# Revit family: console with 2 cutouts for bowl with tap hole
name_source: partatom
category: Furniture
units: mm (PartAtom-declared; Revit-internal decimal feet)

## family parameters
Always vertical = Yes
Cut with Voids When Loaded = No
OmniClass Number = 23.21.19.15.33.13
Room Calculation Point = No
Shared = Yes
Work Plane-Based = No

## types (16) — shared parameters
BIMOBJECT = Sanitary: Compound units
CATALOG = Hansgrohe
DESIGN = Germany
ETIM = EC011381 | Bathroom furniture set
IFC = Furnishing element
L1 = 140
MASTERFORMAT = 12 35 30.23 | Bathroom Casework
Manufacturer = Hansgrohe
NBSYN = $BASENUMBER.-$ARTNR.-$SURFACE.-$LODLEVEL.
NN = Console with 2 cutouts for bowl with tap hole
OBJECTTYPE = Object (single object)
OMNICLASS = 23-19 31 17 11 | Bathroom Units
PRODUCTFAMILY = Xelu Q
PRODUCTGROUP = console
PRODUCTURL = https://pro.hansgrohe.com
REGIONSET = Worldwide
UNICLASS2015 = Pr_40_20_76_94 | Vanity units
UNIFORMATII = E2010 | Fixed Furnishings
UNSPSC = 56 | Furniture and Furnishings

## per-type parameters (varying)
| type | ARTNR | BASENUMBER | GTINCODE | L | LINA | LL | LODLEVEL | Model | NAME | NB | PERMALINK | SPECIFICATION | SURFACE | WEIGHT |
| Console 1360_550 with 2 cutouts for bowl with tap hole-54125050-GLOSSY_WHITE-200 | 54125050 | Console 1360/550 with 2 cutouts for bowl with tap hole | 4059625457856 | 1360 | Console 1360/550 with 2 cutouts for bowl with tap hole-54125050-GLOSSY_WHITE-200 | 270 | 200 | Console 1360/550 with 2 cutouts for bowl with tap hole-54125050-GLOSSY_WHITE-200 | Xelu Q Console 1360/550 with 2 cutouts for bowl with tap hole | Console 1360/550 with 2 cutouts for bowl with tap hole-54125050-GLOSSY_WHITE-200 | 54125XXX | Surfaces:    - 54125050 High Gloss White  - 54125910 Diamond Matt Grey  - 54125230 Natural Oak  - 54125630 Dark Walnut     Specification: | GLOSSY_WHITE | 12 |
| Console 1360_550 with 2 cutouts for bowl with tap hole-54125050-GLOSSY_WHITE-400 | 54125050 | Console 1360/550 with 2 cutouts for bowl with tap hole | 4059625457856 | 1360 | Console 1360/550 with 2 cutouts for bowl with tap hole-54125050-GLOSSY_WHITE-400 | 270 | 400 | Console 1360/550 with 2 cutouts for bowl with tap hole-54125050-GLOSSY_WHITE-400 | Xelu Q Console 1360/550 with 2 cutouts for bowl with tap hole | Console 1360/550 with 2 cutouts for bowl with tap hole-54125050-GLOSSY_WHITE-400 | 54125XXX | Surfaces:    - 54125050 High Gloss White  - 54125910 Diamond Matt Grey  - 54125230 Natural Oak  - 54125630 Dark Walnut     Specification: | GLOSSY_WHITE | 12 |
| Console 1360_550 with 2 cutouts for bowl with tap hole-54125230-NATURAL_OAK-200 | 54125230 | Console 1360/550 with 2 cutouts for bowl with tap hole | 4059625457856 | 1360 | Console 1360/550 with 2 cutouts for bowl with tap hole-54125230-NATURAL_OAK-200 | 270 | 200 | Console 1360/550 with 2 cutouts for bowl with tap hole-54125230-NATURAL_OAK-200 | Xelu Q Console 1360/550 with 2 cutouts for bowl with tap hole | Console 1360/550 with 2 cutouts for bowl with tap hole-54125230-NATURAL_OAK-200 | 54125XXX | Surfaces:    - 54125050 High Gloss White  - 54125910 Diamond Matt Grey  - 54125230 Natural Oak  - 54125630 Dark Walnut     Specification: | NATURAL_OAK | 12 |
| Console 1360_550 with 2 cutouts for bowl with tap hole-54125230-NATURAL_OAK-400 | 54125230 | Console 1360/550 with 2 cutouts for bowl with tap hole | 4059625457856 | 1360 | Console 1360/550 with 2 cutouts for bowl with tap hole-54125230-NATURAL_OAK-400 | 270 | 400 | Console 1360/550 with 2 cutouts for bowl with tap hole-54125230-NATURAL_OAK-400 | Xelu Q Console 1360/550 with 2 cutouts for bowl with tap hole | Console 1360/550 with 2 cutouts for bowl with tap hole-54125230-NATURAL_OAK-400 | 54125XXX | Surfaces:    - 54125050 High Gloss White  - 54125910 Diamond Matt Grey  - 54125230 Natural Oak  - 54125630 Dark Walnut     Specification: | NATURAL_OAK | 12 |
| Console 1360_550 with 2 cutouts for bowl with tap hole-54125630-DARK_WALNUT-200 | 54125630 | Console 1360/550 with 2 cutouts for bowl with tap hole | 4059625457856 | 1360 | Console 1360/550 with 2 cutouts for bowl with tap hole-54125630-DARK_WALNUT-200 | 270 | 200 | Console 1360/550 with 2 cutouts for bowl with tap hole-54125630-DARK_WALNUT-200 | Xelu Q Console 1360/550 with 2 cutouts for bowl with tap hole | Console 1360/550 with 2 cutouts for bowl with tap hole-54125630-DARK_WALNUT-200 | 54125XXX | Surfaces:    - 54125050 High Gloss White  - 54125910 Diamond Matt Grey  - 54125230 Natural Oak  - 54125630 Dark Walnut     Specification: | DARK_WALNUT | 12 |
| Console 1360_550 with 2 cutouts for bowl with tap hole-54125630-DARK_WALNUT-400 | 54125630 | Console 1360/550 with 2 cutouts for bowl with tap hole | 4059625457856 | 1360 | Console 1360/550 with 2 cutouts for bowl with tap hole-54125630-DARK_WALNUT-400 | 270 | 400 | Console 1360/550 with 2 cutouts for bowl with tap hole-54125630-DARK_WALNUT-400 | Xelu Q Console 1360/550 with 2 cutouts for bowl with tap hole | Console 1360/550 with 2 cutouts for bowl with tap hole-54125630-DARK_WALNUT-400 | 54125XXX | Surfaces:    - 54125050 High Gloss White  - 54125910 Diamond Matt Grey  - 54125230 Natural Oak  - 54125630 Dark Walnut     Specification: | DARK_WALNUT | 12 |
| Console 1360_550 with 2 cutouts for bowl with tap hole-54125910-DIAMOND_GREY-200 | 54125910 | Console 1360/550 with 2 cutouts for bowl with tap hole | 4059625457856 | 1360 | Console 1360/550 with 2 cutouts for bowl with tap hole-54125910-DIAMOND_GREY-200 | 270 | 200 | Console 1360/550 with 2 cutouts for bowl with tap hole-54125910-DIAMOND_GREY-200 | Xelu Q Console 1360/550 with 2 cutouts for bowl with tap hole | Console 1360/550 with 2 cutouts for bowl with tap hole-54125910-DIAMOND_GREY-200 | 54125XXX | Surfaces:    - 54125050 High Gloss White  - 54125910 Diamond Matt Grey  - 54125230 Natural Oak  - 54125630 Dark Walnut     Specification: | DIAMOND_GREY | 12 |
| Console 1360_550 with 2 cutouts for bowl with tap hole-54125910-DIAMOND_GREY-400 | 54125910 | Console 1360/550 with 2 cutouts for bowl with tap hole | 4059625457856 | 1360 | Console 1360/550 with 2 cutouts for bowl with tap hole-54125910-DIAMOND_GREY-400 | 270 | 400 | Console 1360/550 with 2 cutouts for bowl with tap hole-54125910-DIAMOND_GREY-400 | Xelu Q Console 1360/550 with 2 cutouts for bowl with tap hole | Console 1360/550 with 2 cutouts for bowl with tap hole-54125910-DIAMOND_GREY-400 | 54125XXX | Surfaces:    - 54125050 High Gloss White  - 54125910 Diamond Matt Grey  - 54125230 Natural Oak  - 54125630 Dark Walnut     Specification: | DIAMOND_GREY | 12 |
| Console 1560_550 with 2 cutouts for bowl with tap hole-54126050-GLOSSY_WHITE-200 | 54126050 | Console 1560/550 with 2 cutouts for bowl with tap hole | 4059625458211 | 1560 | Console 1560/550 with 2 cutouts for bowl with tap hole-54126050-GLOSSY_WHITE-200 | 320 | 200 | Console 1560/550 with 2 cutouts for bowl with tap hole-54126050-GLOSSY_WHITE-200 | Xelu Q Console 1560/550 with 2 cutouts for bowl with tap hole | Console 1560/550 with 2 cutouts for bowl with tap hole-54126050-GLOSSY_WHITE-200 | 54126XXX | Surfaces:    - 54126050 High Gloss White  - 54126910 Diamond Matt Grey  - 54126230 Natural Oak  - 54126630 Dark Walnut      Specification: | GLOSSY_WHITE | 13.3 |
| Console 1560_550 with 2 cutouts for bowl with tap hole-54126050-GLOSSY_WHITE-400 | 54126050 | Console 1560/550 with 2 cutouts for bowl with tap hole | 4059625458211 | 1560 | Console 1560/550 with 2 cutouts for bowl with tap hole-54126050-GLOSSY_WHITE-400 | 320 | 400 | Console 1560/550 with 2 cutouts for bowl with tap hole-54126050-GLOSSY_WHITE-400 | Xelu Q Console 1560/550 with 2 cutouts for bowl with tap hole | Console 1560/550 with 2 cutouts for bowl with tap hole-54126050-GLOSSY_WHITE-400 | 54126XXX | Surfaces:    - 54126050 High Gloss White  - 54126910 Diamond Matt Grey  - 54126230 Natural Oak  - 54126630 Dark Walnut      Specification: | GLOSSY_WHITE | 13.3 |
| Console 1560_550 with 2 cutouts for bowl with tap hole-54126230-NATURAL_OAK-200 | 54126230 | Console 1560/550 with 2 cutouts for bowl with tap hole | 4059625458211 | 1560 | Console 1560/550 with 2 cutouts for bowl with tap hole-54126230-NATURAL_OAK-200 | 320 | 200 | Console 1560/550 with 2 cutouts for bowl with tap hole-54126230-NATURAL_OAK-200 | Xelu Q Console 1560/550 with 2 cutouts for bowl with tap hole | Console 1560/550 with 2 cutouts for bowl with tap hole-54126230-NATURAL_OAK-200 | 54126XXX | Surfaces:    - 54126050 High Gloss White  - 54126910 Diamond Matt Grey  - 54126230 Natural Oak  - 54126630 Dark Walnut      Specification: | NATURAL_OAK | 13.3 |
| Console 1560_550 with 2 cutouts for bowl with tap hole-54126230-NATURAL_OAK-400 | 54126230 | Console 1560/550 with 2 cutouts for bowl with tap hole | 4059625458211 | 1560 | Console 1560/550 with 2 cutouts for bowl with tap hole-54126230-NATURAL_OAK-400 | 320 | 400 | Console 1560/550 with 2 cutouts for bowl with tap hole-54126230-NATURAL_OAK-400 | Xelu Q Console 1560/550 with 2 cutouts for bowl with tap hole | Console 1560/550 with 2 cutouts for bowl with tap hole-54126230-NATURAL_OAK-400 | 54126XXX | Surfaces:    - 54126050 High Gloss White  - 54126910 Diamond Matt Grey  - 54126230 Natural Oak  - 54126630 Dark Walnut      Specification: | NATURAL_OAK | 13.3 |
| Console 1560_550 with 2 cutouts for bowl with tap hole-54126630-DARK_WALNUT-200 | 54126630 | Console 1560/550 with 2 cutouts for bowl with tap hole | 4059625458211 | 1560 | Console 1560/550 with 2 cutouts for bowl with tap hole-54126630-DARK_WALNUT-200 | 320 | 200 | Console 1560/550 with 2 cutouts for bowl with tap hole-54126630-DARK_WALNUT-200 | Xelu Q Console 1560/550 with 2 cutouts for bowl with tap hole | Console 1560/550 with 2 cutouts for bowl with tap hole-54126630-DARK_WALNUT-200 | 54126XXX | Surfaces:    - 54126050 High Gloss White  - 54126910 Diamond Matt Grey  - 54126230 Natural Oak  - 54126630 Dark Walnut      Specification: | DARK_WALNUT | 13.3 |
| Console 1560_550 with 2 cutouts for bowl with tap hole-54126630-DARK_WALNUT-400 | 54126630 | Console 1560/550 with 2 cutouts for bowl with tap hole | 4059625458211 | 1560 | Console 1560/550 with 2 cutouts for bowl with tap hole-54126630-DARK_WALNUT-400 | 320 | 400 | Console 1560/550 with 2 cutouts for bowl with tap hole-54126630-DARK_WALNUT-400 | Xelu Q Console 1560/550 with 2 cutouts for bowl with tap hole | Console 1560/550 with 2 cutouts for bowl with tap hole-54126630-DARK_WALNUT-400 | 54126XXX | Surfaces:    - 54126050 High Gloss White  - 54126910 Diamond Matt Grey  - 54126230 Natural Oak  - 54126630 Dark Walnut      Specification: | DARK_WALNUT | 13.3 |
| Console 1560_550 with 2 cutouts for bowl with tap hole-54126910-DIAMOND_GREY-200 | 54126910 | Console 1560/550 with 2 cutouts for bowl with tap hole | 4059625458211 | 1560 | Console 1560/550 with 2 cutouts for bowl with tap hole-54126910-DIAMOND_GREY-200 | 320 | 200 | Console 1560/550 with 2 cutouts for bowl with tap hole-54126910-DIAMOND_GREY-200 | Xelu Q Console 1560/550 with 2 cutouts for bowl with tap hole | Console 1560/550 with 2 cutouts for bowl with tap hole-54126910-DIAMOND_GREY-200 | 54126XXX | Surfaces:    - 54126050 High Gloss White  - 54126910 Diamond Matt Grey  - 54126230 Natural Oak  - 54126630 Dark Walnut      Specification: | DIAMOND_GREY | 13.3 |
| Console 1560_550 with 2 cutouts for bowl with tap hole-54126910-DIAMOND_GREY-400 | 54126910 | Console 1560/550 with 2 cutouts for bowl with tap hole | 4059625458211 | 1560 | Console 1560/550 with 2 cutouts for bowl with tap hole-54126910-DIAMOND_GREY-400 | 320 | 400 | Console 1560/550 with 2 cutouts for bowl with tap hole-54126910-DIAMOND_GREY-400 | Xelu Q Console 1560/550 with 2 cutouts for bowl with tap hole | Console 1560/550 with 2 cutouts for bowl with tap hole-54126910-DIAMOND_GREY-400 | 54126XXX | Surfaces:    - 54126050 High Gloss White  - 54126910 Diamond Matt Grey  - 54126230 Natural Oak  - 54126630 Dark Walnut      Specification: | DIAMOND_GREY | 13.3 |

type visibility flags: 16 boolean params named "<type name>_RX0RY0RZ0TX0TY0TZ0_V" — each type sets only its own to Yes (folded from table)

## geometry (parser evidence)
native form markers: Sweep x53
no freeform markers — native parametric forms only
